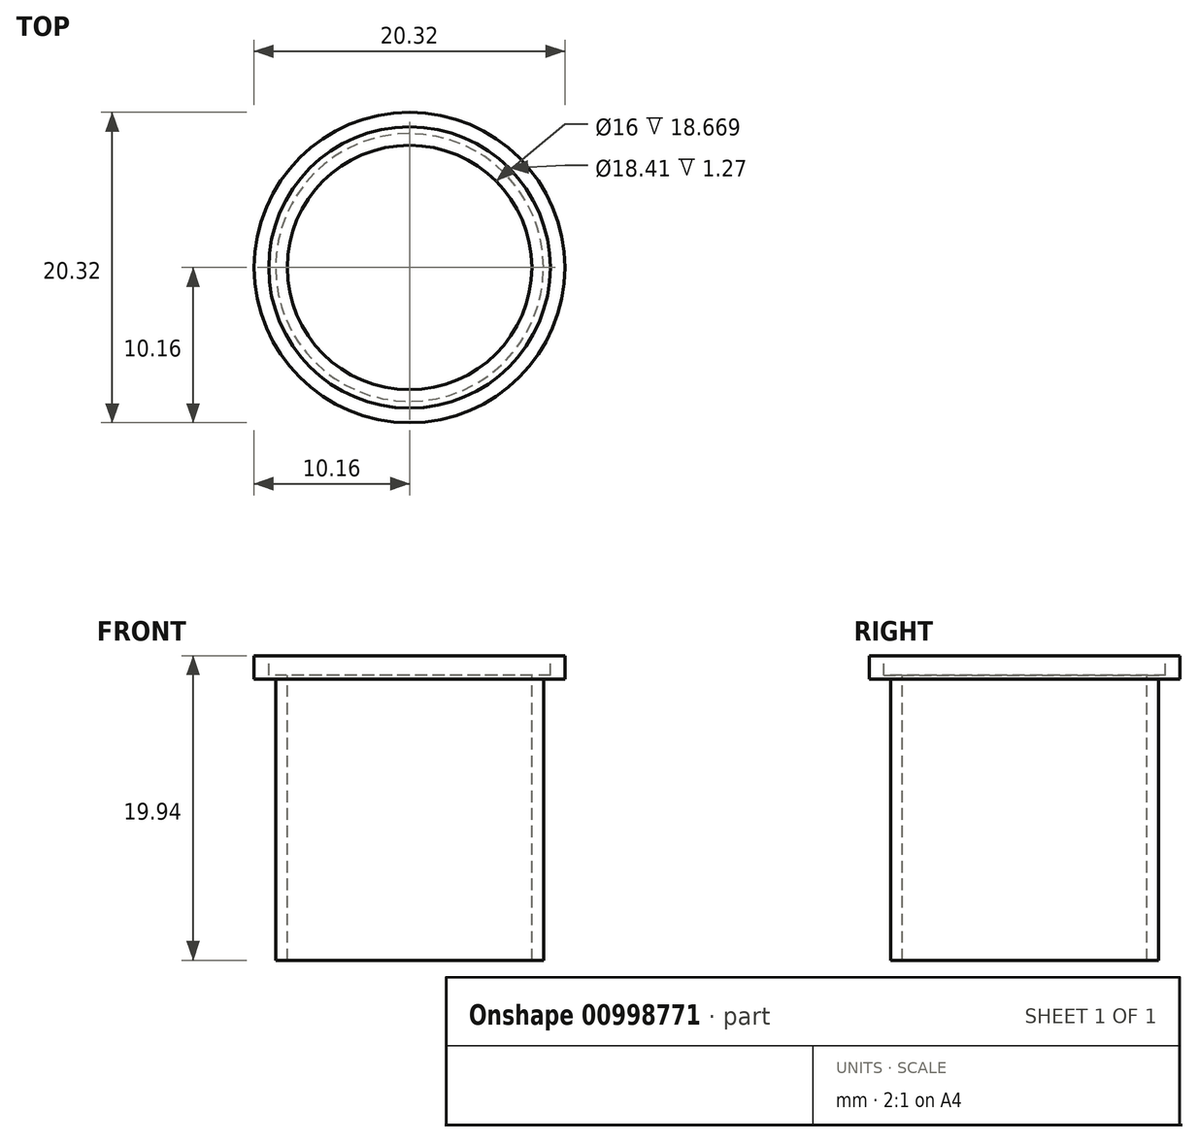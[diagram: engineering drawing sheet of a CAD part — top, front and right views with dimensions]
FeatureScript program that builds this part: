
annotation { "Feature Type Name" : "Feature", "Feature Type Description" : "" }
export const myFeature = defineFeature(function(context is Context, id is Id, definition is map)
    precondition{}
    {
        {
            var Q0;
            Q0=qCreatedBy(makeId("Top.planeOp"),FACE);
            var sketch = newSketch(context, id + "F0", { "sketchPlane" : qUnion([Q0])});
            skCircle(sketch, "E0", {"center": v(0, 0) * mm, "radius": 8.76 * mm});
            skSolve(sketch);
        }
        {
            var Q0;
            Q0 = qSketchRegion(id + "F0", true);
            extrude(context, id + "F1", {"entities" : qUnion([Q0]), "depth" : 18.41 * mm, "offsetDistance" : 25.4 * mm});
        }
        {
            var Q0;
            Q0=makeQuery(id+"F1.opExtrude","CAP_FACE",FACE,{"disambiguationData":[OSD([sQuery(id+"F0.wireOp",EDGE,"E0")])],"isStart":false});
            var sketch = newSketch(context, id + "F2", { "sketchPlane" : qUnion([Q0])});
            skCircle(sketch, "E1", {"center": v(0, 0) * mm, "radius": 8 * mm});
            skSolve(sketch);
        }
        {
            var Q0;
            Q0=makeQuery(id+"F1.opExtrude","CAP_FACE",FACE,{"disambiguationData":[OSD([sQuery(id+"F0.wireOp",EDGE,"E0")])],"isStart":false});
            var sketch = newSketch(context, id + "F3", { "sketchPlane" : qUnion([Q0])});
            skCircle(sketch, "E2", {"center": v(0, 0) * mm, "radius": 10.16 * mm});
            skSolve(sketch);
        }
        {
            var Q0;
            Q0 = qSketchRegion(id + "F3", true);
            extrude(context, id + "F4", {"entities" : qUnion([Q0]), "operationType" : NewBodyOperationType.ADD, "depth" : 1.52 * mm, "offsetDistance" : 25.4 * mm});
        }
        {
            var Q0;
            Q0 = qSketchRegion(id + "F2", true);
            extrude(context, id + "F5", {"entities" : qUnion([Q0]), "operationType" : NewBodyOperationType.REMOVE, "endBound" : BoundingType.SYMMETRIC, "oppositeDirection" : true, "depth" : 55.93 * mm, "offsetDistance" : 25.4 * mm});
        }
        {
            var Q0;
            Q0=makeQuery(id+"F4.opExtrude","CAP_FACE",FACE,{"disambiguationData":[OSD([sQuery(id+"F3.wireOp",EDGE,"E2")])],"isStart":false});
            var sketch = newSketch(context, id + "F6", { "sketchPlane" : qUnion([Q0])});
            skCircle(sketch, "E3", {"center": v(0, 0) * mm, "radius": 9.2 * mm});
            skSolve(sketch);
        }
        {
            var Q0;
            Q0 = qSketchRegion(id + "F6", true);
            extrude(context, id + "F7", {"entities" : qUnion([Q0]), "operationType" : NewBodyOperationType.REMOVE, "oppositeDirection" : true, "depth" : 1.27 * mm, "offsetDistance" : 25.4 * mm});
        }
    });
